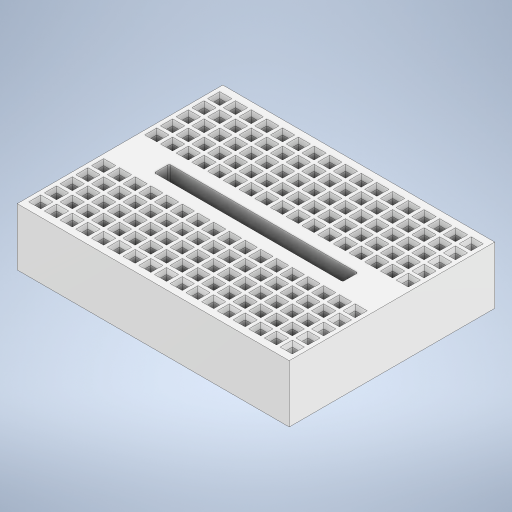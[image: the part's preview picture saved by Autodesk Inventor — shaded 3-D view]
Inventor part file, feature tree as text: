
AUTODESK INVENTOR PART (.ipt)
format: ipt  version: 2024.2 (Build 282272000, 272)  size: 1,050,112 bytes
history: native  units: mm
features: other x1, fillet x1
ambient origin geometry x8: Origin, YZ Plane, XZ Plane, XY Plane, X Axis, Y Axis, Z Axis, Center Point
bodies: Body1 (feature_tree)
feature tree (2):
  other  "Sólido1"
  fillet  "Redondeo4"  [1 undecoded]
note: 1 required parameter value undecoded (feature->parameter linkage not recoverable at this tier; creation-order binding heuristic only, values carry confidence <= 0.55)
